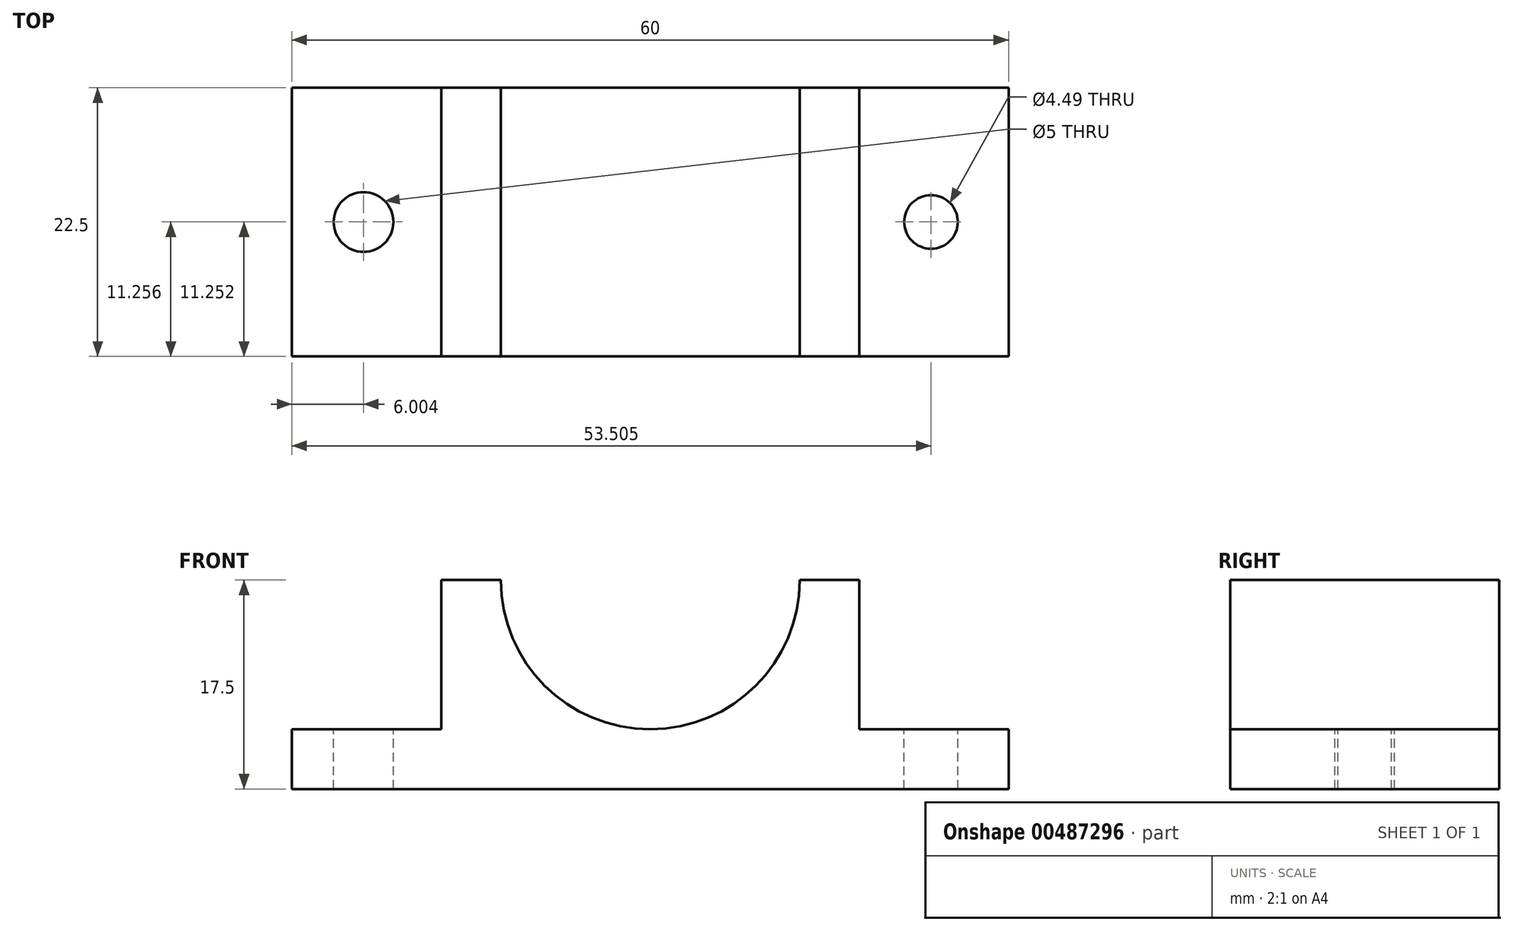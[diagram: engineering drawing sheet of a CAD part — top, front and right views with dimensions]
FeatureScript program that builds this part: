
annotation { "Feature Type Name" : "Feature", "Feature Type Description" : "" }
export const myFeature = defineFeature(function(context is Context, id is Id, definition is map)
    precondition{}
    {
        {
            var Q0;
            Q0=qCreatedBy(makeId("Top.planeOp"),FACE);
            var sketch = newSketch(context, id + "F0", { "sketchPlane" : qUnion([Q0])});
            skLineSegment(sketch, "E0.bottom", {"start": v(-35.7, 6.21) * mm, "end": v(24.3, 6.21) * mm});
            skLineSegment(sketch, "E0.top", {"start": v(-35.7, -16.29) * mm, "end": v(24.3, -16.29) * mm});
            skLineSegment(sketch, "E0.left", {"start": v(-35.7, 6.21) * mm, "end": v(-35.7, -16.29) * mm});
            skLineSegment(sketch, "E0.right", {"start": v(24.3, 6.21) * mm, "end": v(24.3, -16.29) * mm});
            skSolve(sketch);
        }
        {
            var Q0;
            Q0=makeQuery(id+"F0.imprint","IMPRINT",FACE,{"disambiguationData":[TD([[makeQuery(id+"F0.imprint","IMPRINT",EDGE,{"derivedFrom":sQuery(id+"F0.wireOp",EDGE,"E0.bottom")}),-1.0]])]});
            extrude(context, id + "F1", {"entities" : qUnion([Q0]), "depth" : 5 * mm});
        }
        {
            var Q0;
            Q0=makeQuery(id+"F1.opExtrude","CAP_FACE",FACE,{"disambiguationData":[OSD([sQuery(id+"F0.wireOp",EDGE,"E0.bottom"),sQuery(id+"F0.wireOp",EDGE,"E0.top"),sQuery(id+"F0.wireOp",EDGE,"E0.left"),sQuery(id+"F0.wireOp",EDGE,"E0.right")])],"isStart":false});
            var sketch = newSketch(context, id + "F2", { "sketchPlane" : qUnion([Q0])});
            skLineSegment(sketch, "E1", {"start": v(-23.2, 6.21) * mm, "end": v(-23.2, -16.29) * mm});
            skLineSegment(sketch, "E2", {"start": v(11.8, 6.21) * mm, "end": v(11.8, -16.29) * mm});
            skSolve(sketch);
        }
        {
            var Q0;
            {var subQ0=sQuery(id+"F2.wireOp",EDGE,"E1");Q0=makeQuery(id+"F2.imprint","IMPRINT",FACE,{"disambiguationData":[TD([[makeQuery(id+"F2.imprint","IMPRINT",EDGE,{"derivedFrom":subQ0}),1.0]])]});}
            extrude(context, id + "F3", {"entities" : qUnion([Q0]), "operationType" : NewBodyOperationType.ADD, "depth" : 12.5 * mm});
        }
        {
            var Q0;
            {var subQ0=sQuery(id+"F0.wireOp",EDGE,"E0.top");Q0=makeQuery(id+"F3.boolean.opBoolean","MERGE",FACE,{"derivedFrom":[makeQuery(id+"F1.opExtrude","SWEPT_FACE",FACE,{"disambiguationData":[OSD([subQ0])]}),makeQuery(id+"F3.opExtrude","SWEPT_FACE",FACE,{"disambiguationData":[OSD([subQ0])]})]});}
            var sketch = newSketch(context, id + "F4", { "sketchPlane" : qUnion([Q0])});
            skLineSegment(sketch, "E3", {"start": v(-18.2, 17.5) * mm, "end": v(-18.2, 0) * mm});
            skLineSegment(sketch, "E4", {"start": v(6.8, 17.5) * mm, "end": v(6.8, 0) * mm});
            skArc(sketch, "E5", {"start": v(-18.2, 17.5) * mm, "mid": v(-5.7, 5) * mm, "end": v(6.8, 17.5) * mm});
            skSolve(sketch);
        }
        {
            var Q0;
            {var subQ0=sQuery(id+"F4.wireOp",EDGE,"E5");Q0=makeQuery(id+"F4.imprint","IMPRINT",FACE,{"disambiguationData":[TD([[makeQuery(id+"F4.imprint","IMPRINT",EDGE,{"derivedFrom":subQ0}),1.0]])]});}
            extrude(context, id + "F5", {"entities" : qUnion([Q0]), "operationType" : NewBodyOperationType.REMOVE, "endBound" : BoundingType.THROUGH_ALL, "oppositeDirection" : true, "depth" : 25 * mm});
        }
        {
            var Q0;
            {var subQ0=sQuery(id+"F0.wireOp",EDGE,"E0.top");var subQ1=sQuery(id+"F0.wireOp",EDGE,"E0.right");var subQ2=sQuery(id+"F0.wireOp",EDGE,"E0.bottom");Q0=makeQuery(id+"F3.boolean.opBoolean","SPLIT",FACE,{"disambiguationData":[TD([makeQuery(id+"F1.opExtrude","SWEPT_FACE",FACE,{"disambiguationData":[OSD([subQ1])]})])],"derivedFrom":makeQuery(id+"F1.opExtrude","CAP_FACE",FACE,{"disambiguationData":[OSD([subQ2,subQ0,sQuery(id+"F0.wireOp",EDGE,"E0.left"),subQ1])],"isStart":false})});}
            var sketch = newSketch(context, id + "F6", { "sketchPlane" : qUnion([Q0])});
            skCircle(sketch, "E6", {"center": v(17.8, -5.03) * mm, "radius": 2.25 * mm});
            skCircle(sketch, "E7", {"center": v(-29.7, -5.04) * mm, "radius": 2.5 * mm});
            skSolve(sketch);
        }
        {
            var Q0;
            Q0=makeQuery(id+"F6.imprint","IMPRINT",FACE,{"disambiguationData":[TD([[makeQuery(id+"F6.imprint","IMPRINT",EDGE,{"derivedFrom":sQuery(id+"F6.wireOp",EDGE,"E7")}),1.0]])]});
            var Q1;
            Q1=makeQuery(id+"F6.imprint","IMPRINT",FACE,{"disambiguationData":[TD([[makeQuery(id+"F6.imprint","IMPRINT",EDGE,{"derivedFrom":sQuery(id+"F6.wireOp",EDGE,"E6")}),1.0]])]});
            extrude(context, id + "F7", {"entities" : qUnion([Q0, Q1]), "operationType" : NewBodyOperationType.REMOVE, "endBound" : BoundingType.THROUGH_ALL, "oppositeDirection" : true, "depth" : 25 * mm});
        }
    });
